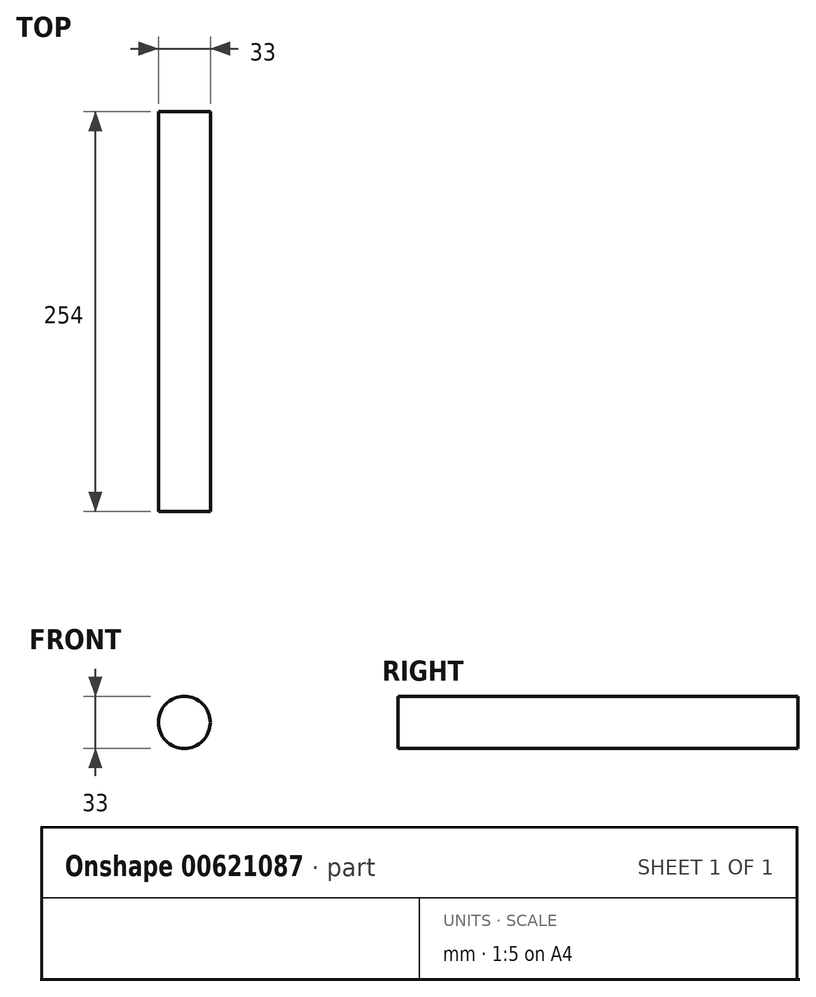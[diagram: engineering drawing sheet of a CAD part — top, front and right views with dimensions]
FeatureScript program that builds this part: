
annotation { "Feature Type Name" : "Feature", "Feature Type Description" : "" }
export const myFeature = defineFeature(function(context is Context, id is Id, definition is map)
    precondition{}
    {
        {
            var Q0;
            Q0=qCreatedBy(makeId("Front.planeOp"),FACE);
            var sketch = newSketch(context, id + "F0", { "sketchPlane" : qUnion([Q0])});
            skCircle(sketch, "E0", {"center": v(0, 0) * mm, "radius": 16.5 * mm});
            skLineSegment(sketch, "E1", {"start": v(0, 0) * mm, "end": v(0, 0) * mm});
            skLineSegment(sketch, "E2", {"start": v(-33.2, 6.9) * mm, "end": v(0, 0) * mm});
            skSolve(sketch);
        }
        {
            var Q0;
            Q0=makeQuery(id+"F0.imprint","IMPRINT",FACE,{"disambiguationData":[TD([[makeQuery(id+"F0.imprint","IMPRINT",EDGE,{"derivedFrom":sQuery(id+"F0.wireOp",EDGE,"E0")}),1.0]])]});
            extrude(context, id + "F1", {"entities" : qUnion([Q0]), "depth" : 254 * mm, "offsetDistance" : 25.4 * mm});
        }
    });
